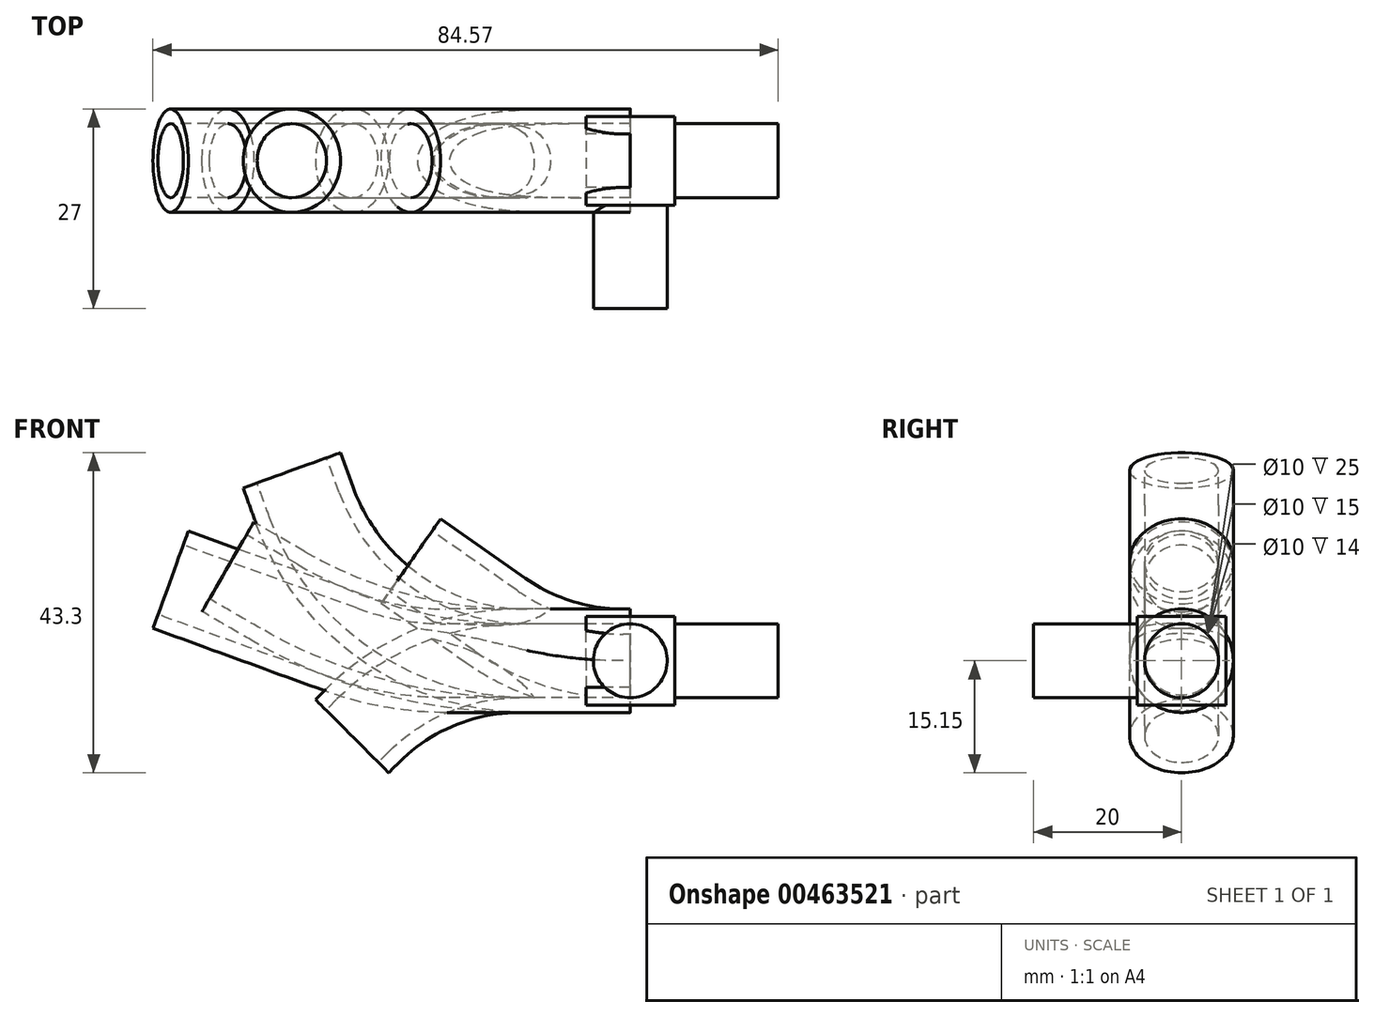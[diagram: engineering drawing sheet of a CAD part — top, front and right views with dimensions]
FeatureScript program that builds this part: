
annotation { "Feature Type Name" : "Feature", "Feature Type Description" : "" }
export const myFeature = defineFeature(function(context is Context, id is Id, definition is map)
    precondition{}
    {
        {
            var Q0;
            Q0=qCreatedBy(makeId("Right.planeOp"),FACE);
            var sketch = newSketch(context, id + "F0", { "sketchPlane" : qUnion([Q0])});
            skCircle(sketch, "E0", {"center": v(0, 0) * mm, "radius": 7 * mm});
            skCircle(sketch, "E1", {"center": v(0, 0) * mm, "radius": 5 * mm});
            skSolve(sketch);
        }
        {
            var Q0;
            Q0=qCreatedBy(makeId("Front.planeOp"),FACE);
            var sketch = newSketch(context, id + "F1", { "sketchPlane" : qUnion([Q0])});
            skLineSegment(sketch, "E2", {"start": v(0, 0) * mm, "end": v(-15, 0) * mm});
            skArc(sketch, "E3", {"start": v(-15, 0) * mm, "mid": v(-26.48, -2.28) * mm, "end": v(-36.21, -8.79) * mm});
            skLineSegment(sketch, "E4", {"start": v(-36.21, -8.79) * mm, "end": v(-37.63, -10.2) * mm});
            skSolve(sketch);
        }
        {
            var Q0;
            Q0=makeQuery(id+"F0.imprint","IMPRINT",FACE,{"disambiguationData":[TD([[makeQuery(id+"F0.imprint","IMPRINT",EDGE,{"derivedFrom":sQuery(id+"F0.wireOp",EDGE,"E0")}),1.0]])]});
            var Q1;
            Q1=sQuery(id+"F1.wireOp",EDGE,"E2");
            var Q2;
            Q2=sQuery(id+"F1.wireOp",EDGE,"E3");
            var Q3;
            Q3=sQuery(id+"F1.wireOp",EDGE,"E4");
            sweep(context, id + "F2", {"profiles" : qUnion([Q0]), "path" : qUnion([Q1, Q2, Q3])});
        }
        {
            var Q0;
            Q0=qCreatedBy(makeId("Front.planeOp"),FACE);
            var sketch = newSketch(context, id + "F3", { "sketchPlane" : qUnion([Q0])});
            skLineSegment(sketch, "E5", {"start": v(0, 0) * mm, "end": v(-1, 0) * mm});
            skArc(sketch, "E6", {"start": v(-18.2, 5.43) * mm, "mid": v(-10.02, 1.39) * mm, "end": v(-1, 0) * mm});
            skLineSegment(sketch, "E7", {"start": v(-18.2, 5.43) * mm, "end": v(-29.68, 13.46) * mm});
            skSolve(sketch);
        }
        {
            var Q0;
            Q0=makeQuery(id+"F0.imprint","IMPRINT",FACE,{"disambiguationData":[TD([[makeQuery(id+"F0.imprint","IMPRINT",EDGE,{"derivedFrom":sQuery(id+"F0.wireOp",EDGE,"E0")}),1.0]])]});
            var Q1;
            Q1=sQuery(id+"F3.wireOp",EDGE,"E5");
            var Q2;
            Q2=sQuery(id+"F3.wireOp",EDGE,"E6");
            var Q3;
            Q3=sQuery(id+"F3.wireOp",EDGE,"E7");
            sweep(context, id + "F4", {"profiles" : qUnion([Q0]), "path" : qUnion([Q1, Q2, Q3])});
        }
        {
            var Q0;
            Q0=qCreatedBy(makeId("Front.planeOp"),FACE);
            var sketch = newSketch(context, id + "F5", { "sketchPlane" : qUnion([Q0])});
            skLineSegment(sketch, "E8.bottom", {"start": v(-6, 6) * mm, "end": v(6, 6) * mm});
            skLineSegment(sketch, "E8.top", {"start": v(-6, -6) * mm, "end": v(6, -6) * mm});
            skLineSegment(sketch, "E8.left", {"start": v(-6, 6) * mm, "end": v(-6, -6) * mm});
            skLineSegment(sketch, "E8.right", {"start": v(6, 6) * mm, "end": v(6, -6) * mm});
            skSolve(sketch);
        }
        {
            var Q0;
            Q0=makeQuery(id+"F5.imprint","IMPRINT",FACE,{"disambiguationData":[TD([[makeQuery(id+"F5.imprint","IMPRINT",EDGE,{"derivedFrom":sQuery(id+"F5.wireOp",EDGE,"E8.bottom")}),-1.0]])]});
            extrude(context, id + "F6", {"entities" : qUnion([Q0]), "depth" : 12 * mm, "offsetDistance" : 25 * mm, "symmetric" : true});
        }
        {
            var Q0;
            Q0=makeQuery(id+"F6.opExtrude","CAP_FACE",FACE,{"disambiguationData":[OSD([sQuery(id+"F5.wireOp",EDGE,"E8.bottom"),sQuery(id+"F5.wireOp",EDGE,"E8.top"),sQuery(id+"F5.wireOp",EDGE,"E8.left"),sQuery(id+"F5.wireOp",EDGE,"E8.right")])],"isStart":false});
            var sketch = newSketch(context, id + "F7", { "sketchPlane" : qUnion([Q0])});
            skCircle(sketch, "E9", {"center": v(0, 0) * mm, "radius": 5 * mm});
            skSolve(sketch);
        }
        {
            var Q0;
            Q0=makeQuery(id+"F7.imprint","IMPRINT",FACE,{"disambiguationData":[TD([[makeQuery(id+"F7.imprint","IMPRINT",EDGE,{"derivedFrom":sQuery(id+"F7.wireOp",EDGE,"E9")}),1.0]])]});
            extrude(context, id + "F8", {"entities" : qUnion([Q0]), "operationType" : NewBodyOperationType.ADD, "depth" : 14 * mm, "offsetDistance" : 25 * mm});
        }
        {
            var Q0;
            Q0=makeQuery(id+"F6.opExtrude","SWEPT_FACE",FACE,{"disambiguationData":[OSD([sQuery(id+"F5.wireOp",EDGE,"E8.right")])]});
            var sketch = newSketch(context, id + "F9", { "sketchPlane" : qUnion([Q0])});
            skCircle(sketch, "E10", {"center": v(0, 0) * mm, "radius": 5 * mm});
            skSolve(sketch);
        }
        {
            var Q0;
            Q0=makeQuery(id+"F9.imprint","IMPRINT",FACE,{"disambiguationData":[TD([[makeQuery(id+"F9.imprint","IMPRINT",EDGE,{"derivedFrom":sQuery(id+"F9.wireOp",EDGE,"E10")}),1.0]])]});
            extrude(context, id + "F10", {"entities" : qUnion([Q0]), "operationType" : NewBodyOperationType.ADD, "depth" : 14 * mm, "offsetDistance" : 25 * mm});
        }
        {
            var Q0;
            Q0=qCreatedBy(makeId("Front.planeOp"),FACE);
            var sketch = newSketch(context, id + "F11", { "sketchPlane" : qUnion([Q0])});
            skLineSegment(sketch, "E11", {"start": v(0, 0) * mm, "end": v(-14, 0) * mm});
            skLineSegment(sketch, "E12", {"start": v(-45.78, 25.75) * mm, "end": v(-44.07, 21.06) * mm});
            skArc(sketch, "E13", {"start": v(-44.07, 21.06) * mm, "mid": v(-32.35, 5.79) * mm, "end": v(-14, 0) * mm});
            skSolve(sketch);
        }
        {
            var Q0;
            Q0=makeQuery(id+"F0.imprint","IMPRINT",FACE,{"disambiguationData":[TD([[makeQuery(id+"F0.imprint","IMPRINT",EDGE,{"derivedFrom":sQuery(id+"F0.wireOp",EDGE,"E0")}),1.0]])]});
            var Q1;
            Q1=sQuery(id+"F11.wireOp",EDGE,"E11");
            var Q2;
            Q2=sQuery(id+"F11.wireOp",EDGE,"E13");
            var Q3;
            Q3=sQuery(id+"F11.wireOp",EDGE,"E12");
            sweep(context, id + "F12", {"profiles" : qUnion([Q0]), "path" : qUnion([Q1, Q2, Q3])});
        }
        {
            var Q0;
            Q0=qCreatedBy(makeId("Front.planeOp"),FACE);
            var sketch = newSketch(context, id + "F13", { "sketchPlane" : qUnion([Q0])});
            skLineSegment(sketch, "E14", {"start": v(0, 0) * mm, "end": v(-25, 0) * mm});
            skLineSegment(sketch, "E15", {"start": v(-62.17, 10.96) * mm, "end": v(-38.68, 2.41) * mm});
            skArc(sketch, "E16", {"start": v(-38.68, 2.41) * mm, "mid": v(-31.95, 0.6) * mm, "end": v(-25, 0) * mm});
            skSolve(sketch);
        }
        {
            var Q0;
            Q0=makeQuery(id+"F0.imprint","IMPRINT",FACE,{"disambiguationData":[TD([[makeQuery(id+"F0.imprint","IMPRINT",EDGE,{"derivedFrom":sQuery(id+"F0.wireOp",EDGE,"E0")}),1.0]])]});
            var Q1;
            Q1=sQuery(id+"F13.wireOp",EDGE,"E14");
            var Q2;
            Q2=sQuery(id+"F13.wireOp",EDGE,"E16");
            var Q3;
            Q3=sQuery(id+"F13.wireOp",EDGE,"E15");
            sweep(context, id + "F14", {"profiles" : qUnion([Q0]), "path" : qUnion([Q1, Q2, Q3])});
        }
        {
            var Q0;
            Q0=qCreatedBy(makeId("Front.planeOp"),FACE);
            var sketch = newSketch(context, id + "F15", { "sketchPlane" : qUnion([Q0])});
            skLineSegment(sketch, "E17", {"start": v(0, 0) * mm, "end": v(-15, 0) * mm});
            skLineSegment(sketch, "E18", {"start": v(-54.43, 12.7) * mm, "end": v(-47.5, 8.7) * mm});
            skArc(sketch, "E19", {"start": v(-47.5, 8.7) * mm, "mid": v(-31.82, 2.21) * mm, "end": v(-15, 0) * mm});
            skSolve(sketch);
        }
        {
            var Q0;
            Q0 = qSketchRegion(id + "F15", true);
            var Q1;
            Q1=makeQuery(id+"F0.imprint","IMPRINT",FACE,{"disambiguationData":[TD([[makeQuery(id+"F0.imprint","IMPRINT",EDGE,{"derivedFrom":sQuery(id+"F0.wireOp",EDGE,"E0")}),1.0]])]});
            var Q2;
            Q2=sQuery(id+"F15.wireOp",EDGE,"E17");
            var Q3;
            Q3=sQuery(id+"F15.wireOp",EDGE,"E19");
            var Q4;
            Q4=sQuery(id+"F15.wireOp",EDGE,"E18");
            sweep(context, id + "F16", {"profiles" : qUnion([Q0, Q1]), "path" : qUnion([Q2, Q3, Q4])});
        }
    });
